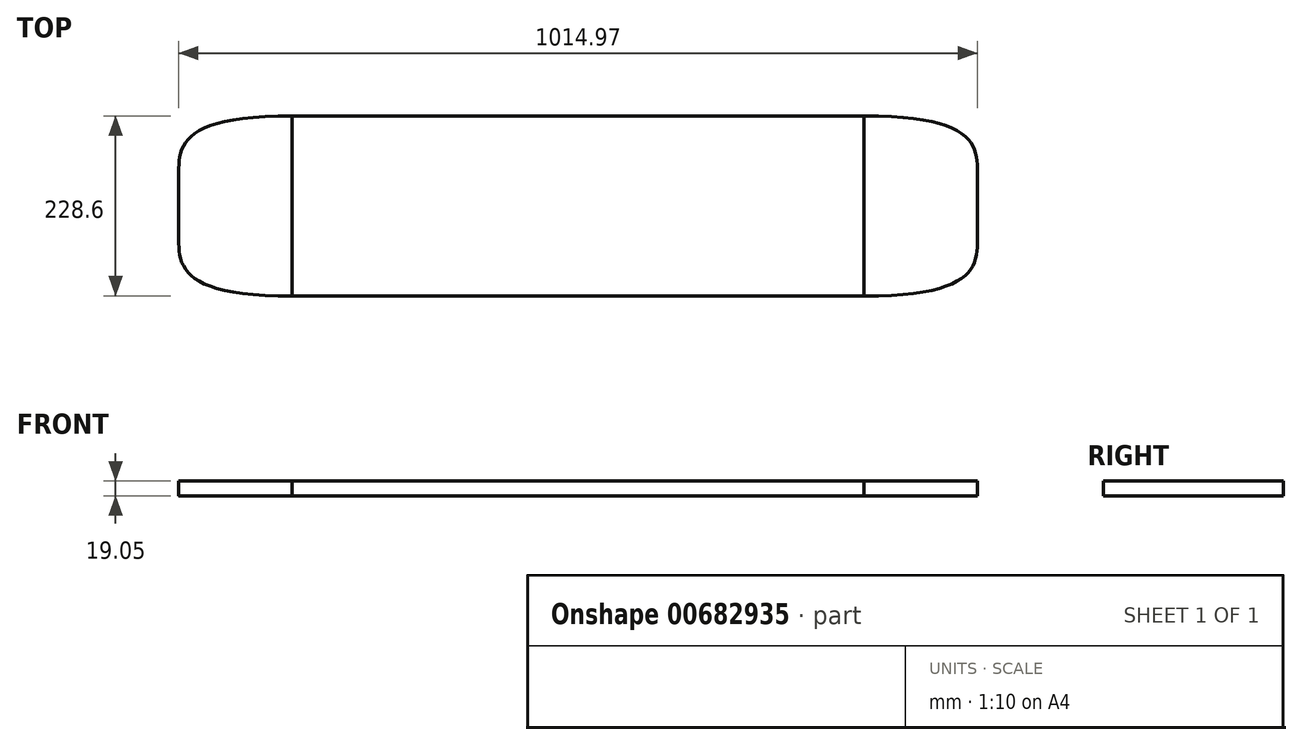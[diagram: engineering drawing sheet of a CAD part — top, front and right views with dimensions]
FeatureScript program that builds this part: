
annotation { "Feature Type Name" : "Feature", "Feature Type Description" : "" }
export const myFeature = defineFeature(function(context is Context, id is Id, definition is map)
    precondition{}
    {
        {
            var Q0;
            Q0=qCreatedBy(makeId("Top.planeOp"),FACE);
            var sketch = newSketch(context, id + "F0", { "sketchPlane" : qUnion([Q0])});
            skLineSegment(sketch, "E0.bottom", {"start": v(-508, -114.3) * mm, "end": v(508, -114.3) * mm});
            skLineSegment(sketch, "E0.top", {"start": v(-508, 114.3) * mm, "end": v(508, 114.3) * mm});
            skLineSegment(sketch, "E0.left", {"start": v(-508, -114.3) * mm, "end": v(-508, 114.3) * mm});
            skLineSegment(sketch, "E0.right", {"start": v(508, -114.3) * mm, "end": v(508, 114.3) * mm});
            skPoint(sketch, "E0.middle", {"position": v(0, 0) * mm});
            skLineSegment(sketch, "E1", {"start": v(363.72, 114.3) * mm, "end": v(363.72, -114.3) * mm});
            skFitSpline(sketch, "E2", {"points": [v(363.72, 114.3) * mm, v(508, 38.1) * mm, v(508, -38.1) * mm, v(363.72, -114.3) * mm], "startDerivative": vector(1161.46, 0) * mm, "endDerivative": vector(-1161.46, 0) * mm});
            skLineSegment(sketch, "E3", {"start": v(508, 114.3) * mm, "end": v(508, 38.1) * mm});
            skLineSegment(sketch, "E4", {"start": v(508, -114.3) * mm, "end": v(508, -38.1) * mm});
            skLineSegment(sketch, "E5.right", {"start": v(-506.97, 114.3) * mm, "end": v(-506.97, -114.3) * mm});
            skLineSegment(sketch, "E6", {"start": v(-362.69, -114.3) * mm, "end": v(-362.69, 114.3) * mm});
            skFitSpline(sketch, "E7", {"points": [v(-362.69, -114.3) * mm, v(-506.97, -38.1) * mm, v(-506.97, 38.1) * mm, v(-362.69, 114.3) * mm], "startDerivative": vector(-1161.46, 0) * mm, "endDerivative": vector(1161.46, 0) * mm});
            skLineSegment(sketch, "E8", {"start": v(-506.97, -114.3) * mm, "end": v(-506.97, -38.1) * mm});
            skLineSegment(sketch, "E9", {"start": v(-506.97, 114.3) * mm, "end": v(-506.97, 38.1) * mm});
            skSolve(sketch);
        }
        {
            var Q0;
            {var subQ1=sQuery(id+"F0.wireOp",EDGE,"E1");Q0=makeQuery(id+"F0.imprint","IMPRINT",FACE,{"disambiguationData":[TD([[makeQuery(id+"F0.imprint","IMPRINT",EDGE,{"derivedFrom":subQ1}),-1.0]])]});}
            extrude(context, id + "F1", {"entities" : qUnion([Q0]), "depth" : 19.05 * mm, "offsetDistance" : 25.4 * mm});
        }
        {
            var Q0;
            {var subQ0=sQuery(id+"F0.wireOp",EDGE,"E1");Q0=makeQuery(id+"F0.imprint","IMPRINT",FACE,{"disambiguationData":[TD([[makeQuery(id+"F0.imprint","IMPRINT",EDGE,{"derivedFrom":subQ0}),1.0]])]});}
            var Q1;
            {var subQ5=sQuery(id+"F0.wireOp",EDGE,"E6");Q1=makeQuery(id+"F0.imprint","IMPRINT",FACE,{"disambiguationData":[TD([[makeQuery(id+"F0.imprint","IMPRINT",EDGE,{"derivedFrom":subQ5}),1.0]])]});}
            extrude(context, id + "F2", {"entities" : qUnion([Q0, Q1]), "depth" : 19.05 * mm, "offsetDistance" : 25.4 * mm});
        }
    });
